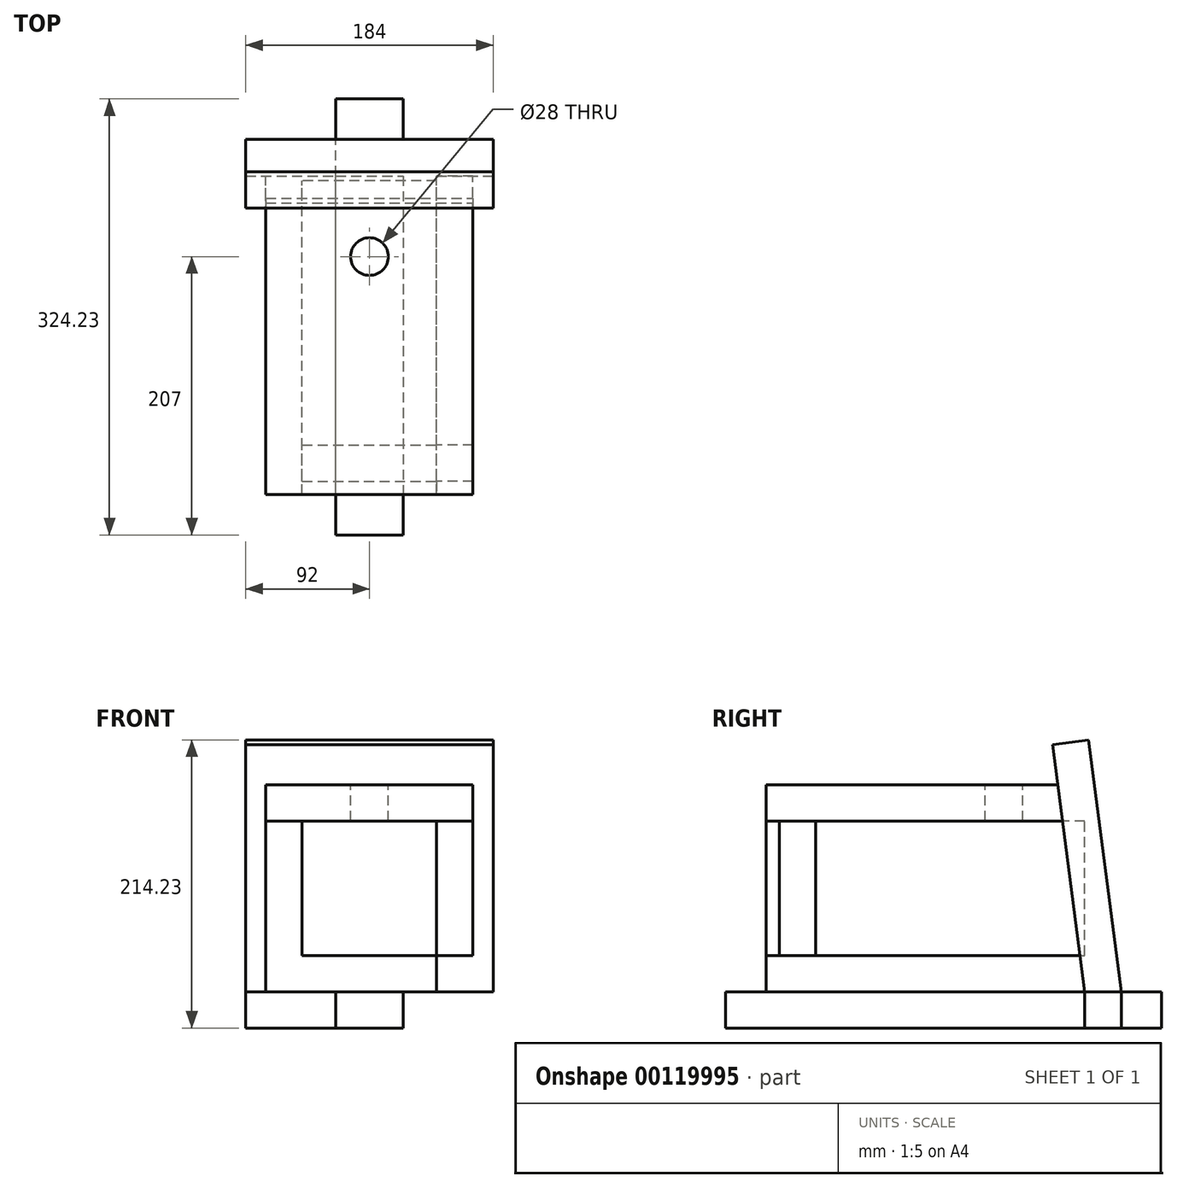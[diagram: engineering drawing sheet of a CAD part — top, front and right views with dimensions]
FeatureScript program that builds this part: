
annotation { "Feature Type Name" : "Feature", "Feature Type Description" : "" }
export const myFeature = defineFeature(function(context is Context, id is Id, definition is map)
    precondition{}
    {
        {
            var Q0;
            Q0=qCreatedBy(makeId("Top.planeOp"),FACE);
            var sketch = newSketch(context, id + "F0", { "sketchPlane" : qUnion([Q0])});
            skLineSegment(sketch, "E0.bottom", {"start": v(0, 0) * mm, "end": v(100, 0) * mm});
            skLineSegment(sketch, "E0.top", {"start": v(0, 237) * mm, "end": v(100, 237) * mm});
            skLineSegment(sketch, "E0.left", {"start": v(0, 0) * mm, "end": v(0, 237) * mm});
            skLineSegment(sketch, "E0.right", {"start": v(100, 0) * mm, "end": v(100, 237) * mm});
            skSolve(sketch);
        }
        {
            var Q0;
            Q0 = qSketchRegion(id + "F0", true);
            var Q1;
            Q1=makeQuery(id+"F0.imprint","IMPRINT",FACE,{"disambiguationData":[TD([[makeQuery(id+"F0.imprint","IMPRINT",EDGE,{"derivedFrom":sQuery(id+"F0.wireOp",EDGE,"E0.bottom")}),1.0]])]});
            extrude(context, id + "F1", {"entities" : qUnion([Q0, Q1]), "depth" : 27 * mm});
        }
        {
            var Q0;
            Q0=makeQuery(id+"F1.opExtrude","CAP_FACE",FACE,{"disambiguationData":[OSD([sQuery(id+"F0.wireOp",EDGE,"E0.bottom"),sQuery(id+"F0.wireOp",EDGE,"E0.top"),sQuery(id+"F0.wireOp",EDGE,"E0.left"),sQuery(id+"F0.wireOp",EDGE,"E0.right")])],"isStart":false});
            var sketch = newSketch(context, id + "F2", { "sketchPlane" : qUnion([Q0])});
            skLineSegment(sketch, "E1.bottom", {"start": v(0, 37) * mm, "end": v(100, 37) * mm});
            skLineSegment(sketch, "E1.top", {"start": v(0, 10) * mm, "end": v(100, 10) * mm});
            skLineSegment(sketch, "E1.left", {"start": v(0, 37) * mm, "end": v(0, 10) * mm});
            skLineSegment(sketch, "E1.right", {"start": v(100, 37) * mm, "end": v(100, 10) * mm});
            skSolve(sketch);
        }
        {
            var Q0;
            Q0 = qSketchRegion(id + "F2", true);
            extrude(context, id + "F3", {"entities" : qUnion([Q0]), "depth" : 100 * mm});
        }
        {
            var Q0;
            Q0=makeQuery(id+"F1.opExtrude","SWEPT_FACE",FACE,{"disambiguationData":[OSD([sQuery(id+"F0.wireOp",EDGE,"E0.right")])]});
            var sketch = newSketch(context, id + "F4", { "sketchPlane" : qUnion([Q0])});
            skLineSegment(sketch, "E2.0.0", {"start": v(0, 0) * mm, "end": v(237, 0) * mm});
            skLineSegment(sketch, "E2.0.1", {"start": v(237, 0) * mm, "end": v(237, 27) * mm});
            skLineSegment(sketch, "E2.0.2", {"start": v(237, 27) * mm, "end": v(0, 27) * mm});
            skLineSegment(sketch, "E2.0.3", {"start": v(0, 27) * mm, "end": v(0, 0) * mm});
            skLineSegment(sketch, "E3.0.0", {"start": v(10, 27) * mm, "end": v(37, 27) * mm});
            skLineSegment(sketch, "E3.0.1", {"start": v(37, 27) * mm, "end": v(37, 127) * mm});
            skLineSegment(sketch, "E3.0.2", {"start": v(37, 127) * mm, "end": v(10, 127) * mm});
            skLineSegment(sketch, "E3.0.3", {"start": v(10, 127) * mm, "end": v(10, 27) * mm});
            skLineSegment(sketch, "E4.bottom", {"start": v(237, 0) * mm, "end": v(0, 0) * mm});
            skLineSegment(sketch, "E4.top", {"start": v(237, 127) * mm, "end": v(0, 127) * mm});
            skLineSegment(sketch, "E4.left", {"start": v(237, 0) * mm, "end": v(237, 127) * mm});
            skLineSegment(sketch, "E4.right", {"start": v(0, 0) * mm, "end": v(0, 127) * mm});
            skSolve(sketch);
        }
        {
            var Q0;
            {var subQ1=sQuery(id+"F4.wireOp",EDGE,"E3.0.0");Q0=makeQuery(id+"F4.imprint","IMPRINT",FACE,{"disambiguationData":[TD([[makeQuery(id+"F4.imprint","IMPRINT",EDGE,{"derivedFrom":subQ1}),-1.0]])]});}
            var Q1;
            {var subQ3=sQuery(id+"F4.wireOp",EDGE,"E3.0.1");Q1=makeQuery(id+"F4.imprint","IMPRINT",FACE,{"disambiguationData":[TD([[makeQuery(id+"F4.imprint","IMPRINT",EDGE,{"derivedFrom":subQ3}),-1.0]])]});}
            var Q2;
            Q2=makeQuery(id+"F4.imprint","IMPRINT",FACE,{"disambiguationData":[TD([[makeQuery(id+"F4.imprint","IMPRINT",EDGE,{"derivedFrom":sQuery(id+"F4.wireOp",EDGE,"E3.0.0")}),1.0]])]});
            var Q3;
            {var subQ3=sQuery(id+"F4.wireOp",EDGE,"E3.0.3");Q3=makeQuery(id+"F4.imprint","IMPRINT",FACE,{"disambiguationData":[TD([[makeQuery(id+"F4.imprint","IMPRINT",EDGE,{"derivedFrom":subQ3}),-1.0]])]});}
            extrude(context, id + "F5", {"entities" : qUnion([Q0, Q1, Q2, Q3]), "depth" : 27 * mm});
        }
        {
            var Q0;
            Q0=makeQuery(id+"F5.opExtrude","SWEPT_FACE",FACE,{"disambiguationData":[OSD([sQuery(id+"F4.wireOp",EDGE,"E4.top")])]});
            var sketch = newSketch(context, id + "F6", { "sketchPlane" : qUnion([Q0])});
            skLineSegment(sketch, "E5.bottom", {"start": v(127, 237) * mm, "end": v(-27, 237) * mm});
            skLineSegment(sketch, "E5.top", {"start": v(127, 0) * mm, "end": v(-27, 0) * mm});
            skLineSegment(sketch, "E5.left", {"start": v(127, 237) * mm, "end": v(127, 0) * mm});
            skLineSegment(sketch, "E5.right", {"start": v(-27, 237) * mm, "end": v(-27, 0) * mm});
            skSolve(sketch);
        }
        {
            var Q0;
            {var subQ2=sQuery(id+"F6.wireOp",EDGE,"E5.left");Q0=makeQuery(id+"F6.imprint","IMPRINT",FACE,{"disambiguationData":[TD([[makeQuery(id+"F6.imprint","IMPRINT",EDGE,{"derivedFrom":subQ2}),-1.0]])]});}
            var Q1;
            {var subQ2=sQuery(id+"F6.wireOp",EDGE,"E5.right");Q1=makeQuery(id+"F6.imprint","IMPRINT",FACE,{"disambiguationData":[TD([[makeQuery(id+"F6.imprint","IMPRINT",EDGE,{"derivedFrom":subQ2}),1.0]])]});}
            extrude(context, id + "F7", {"entities" : qUnion([Q0, Q1]), "depth" : 27 * mm});
        }
        {
            var Q0;
            Q0=makeQuery(id+"F7.opExtrude","CAP_FACE",FACE,{"disambiguationData":[OSD([sQuery(id+"F6.wireOp",EDGE,"E5.bottom"),sQuery(id+"F6.wireOp",EDGE,"E5.top"),sQuery(id+"F6.wireOp",EDGE,"E5.left"),sQuery(id+"F6.wireOp",EDGE,"E5.right")])],"isStart":false});
            var sketch = newSketch(context, id + "F8", { "sketchPlane" : qUnion([Q0])});
            skLineSegment(sketch, "E6.0.1", {"start": v(100, 237) * mm, "end": v(100, 0) * mm});
            skLineSegment(sketch, "E6.0.3", {"start": v(100, 0) * mm, "end": v(100, 237) * mm});
            skLineSegment(sketch, "E7.0.0", {"start": v(0, 37) * mm, "end": v(0, 10) * mm});
            skLineSegment(sketch, "E7.0.2", {"start": v(0, 10) * mm, "end": v(0, 37) * mm});
            skCircle(sketch, "E8", {"center": v(50, 177) * mm, "radius": 14 * mm});
            skPoint(sketch, "E8.centerSnap0", {"position": v(50, 0) * mm});
            skSolve(sketch);
        }
        {
            var Q0;
            Q0=makeQuery(id+"F8.imprint","IMPRINT",FACE,{"disambiguationData":[TD([[makeQuery(id+"F8.imprint","IMPRINT",EDGE,{"derivedFrom":sQuery(id+"F8.wireOp",EDGE,"E8")}),1.0]])]});
            extrude(context, id + "F9", {"entities" : qUnion([Q0]), "operationType" : NewBodyOperationType.REMOVE, "endBound" : BoundingType.UP_TO_NEXT, "oppositeDirection" : true, "depth" : 25 * mm});
        }
        {
            var Q0;
            Q0=makeQuery(id+"F5.opExtrude","CAP_FACE",FACE,{"disambiguationData":[OSD([sQuery(id+"F4.wireOp",EDGE,"E4.bottom"),sQuery(id+"F4.wireOp",EDGE,"E4.top"),sQuery(id+"F4.wireOp",EDGE,"E4.left"),sQuery(id+"F4.wireOp",EDGE,"E4.right")])],"isStart":false});
            var sketch = newSketch(context, id + "F10", { "sketchPlane" : qUnion([Q0])});
            skLineSegment(sketch, "E9.0.0", {"start": v(0, 127) * mm, "end": v(237, 127) * mm});
            skLineSegment(sketch, "E9.0.1", {"start": v(237, 127) * mm, "end": v(237, 154) * mm});
            skLineSegment(sketch, "E9.0.2", {"start": v(237, 154) * mm, "end": v(0, 154) * mm});
            skLineSegment(sketch, "E9.0.3", {"start": v(0, 154) * mm, "end": v(0, 127) * mm});
            skLineSegment(sketch, "E10.0.0", {"start": v(237, 0) * mm, "end": v(237, 127) * mm});
            skLineSegment(sketch, "E10.0.1", {"start": v(237, 127) * mm, "end": v(0, 127) * mm});
            skLineSegment(sketch, "E10.0.2", {"start": v(0, 127) * mm, "end": v(0, 0) * mm});
            skLineSegment(sketch, "E10.0.3", {"start": v(0, 0) * mm, "end": v(237, 0) * mm});
            skLineSegment(sketch, "E11", {"start": v(237, 0) * mm, "end": v(217, 154) * mm});
            skSolve(sketch);
        }
        {
            var Q0;
            {var subQ0=sQuery(id+"F10.wireOp",EDGE,"E10.0.0");Q0=makeQuery(id+"F10.imprint","IMPRINT",FACE,{"disambiguationData":[TD([[makeQuery(id+"F10.imprint","IMPRINT",EDGE,{"derivedFrom":subQ0}),-1.0]])]});}
            var Q1;
            {var subQ0=sQuery(id+"F10.wireOp",EDGE,"E9.0.1");Q1=makeQuery(id+"F10.imprint","IMPRINT",FACE,{"disambiguationData":[TD([[makeQuery(id+"F10.imprint","IMPRINT",EDGE,{"derivedFrom":subQ0}),1.0]])]});}
            extrude(context, id + "F11", {"entities" : qUnion([Q0, Q1]), "operationType" : NewBodyOperationType.REMOVE, "endBound" : BoundingType.THROUGH_ALL, "oppositeDirection" : true, "depth" : 25 * mm});
        }
        {
            var Q0;
            Q0=makeQuery(id+"F1.opExtrude","SWEPT_FACE",FACE,{"disambiguationData":[OSD([sQuery(id+"F0.wireOp",EDGE,"E0.left")])]});
            var sketch = newSketch(context, id + "F12", { "sketchPlane" : qUnion([Q0])});
            skLineSegment(sketch, "E12.0.0", {"start": v(-220.5, 127) * mm, "end": v(-237, 0) * mm});
            skLineSegment(sketch, "E12.0.1", {"start": v(-237, 0) * mm, "end": v(0, 0) * mm});
            skLineSegment(sketch, "E12.0.2", {"start": v(0, 0) * mm, "end": v(0, 127) * mm});
            skLineSegment(sketch, "E12.0.3", {"start": v(0, 127) * mm, "end": v(-220.5, 127) * mm});
            skSolve(sketch);
        }
        {
            var Q0;
            {var subQ2=sQuery(id+"F12.wireOp",EDGE,"E12.0.3");Q0=makeQuery(id+"F12.imprint","IMPRINT",FACE,{"disambiguationData":[TD([[makeQuery(id+"F12.imprint","IMPRINT",EDGE,{"derivedFrom":subQ2}),1.0]])]});}
            var Q1;
            {var subQ0=sQuery(id+"F12.wireOp",EDGE,"E12.0.1");Q1=makeQuery(id+"F12.imprint","IMPRINT",FACE,{"disambiguationData":[TD([[makeQuery(id+"F12.imprint","IMPRINT",EDGE,{"derivedFrom":subQ0}),-1.0]])]});}
            extrude(context, id + "F13", {"entities" : qUnion([Q0, Q1]), "depth" : 27 * mm});
        }
        {
            var Q0;
            Q0=makeQuery(id+"F13.opExtrude","SWEPT_FACE",FACE,{"disambiguationData":[OSD([sQuery(id+"F12.wireOp",EDGE,"E12.0.0")])]});
            var sketch = newSketch(context, id + "F14", { "sketchPlane" : qUnion([Q0])});
            skLineSegment(sketch, "E13.0.0", {"start": v(27, 97.54) * mm, "end": v(27, 124.77) * mm});
            skLineSegment(sketch, "E13.0.1", {"start": v(27, 124.77) * mm, "end": v(-127, 124.77) * mm});
            skLineSegment(sketch, "E13.0.2", {"start": v(-127, 124.77) * mm, "end": v(-127, 97.54) * mm});
            skLineSegment(sketch, "E13.0.3", {"start": v(-127, 97.54) * mm, "end": v(27, 97.54) * mm});
            skLineSegment(sketch, "E14.0.0", {"start": v(-100, 97.54) * mm, "end": v(-127, 97.54) * mm});
            skLineSegment(sketch, "E14.0.1", {"start": v(-127, 97.54) * mm, "end": v(-127, -30.52) * mm});
            skLineSegment(sketch, "E14.0.2", {"start": v(-127, -30.52) * mm, "end": v(-100, -30.52) * mm});
            skLineSegment(sketch, "E14.0.3", {"start": v(-100, -30.52) * mm, "end": v(-100, 97.54) * mm});
            skLineSegment(sketch, "E15.0.0", {"start": v(0, -3.3) * mm, "end": v(-100, -3.3) * mm});
            skLineSegment(sketch, "E15.0.1", {"start": v(-100, -3.3) * mm, "end": v(-100, -30.52) * mm});
            skLineSegment(sketch, "E15.0.2", {"start": v(-100, -30.52) * mm, "end": v(0, -30.52) * mm});
            skLineSegment(sketch, "E15.0.3", {"start": v(0, -30.52) * mm, "end": v(0, -3.3) * mm});
            skLineSegment(sketch, "E16.0.0", {"start": v(0, 97.54) * mm, "end": v(0, -30.52) * mm});
            skLineSegment(sketch, "E16.0.1", {"start": v(0, -30.52) * mm, "end": v(27, -30.52) * mm});
            skLineSegment(sketch, "E16.0.2", {"start": v(27, -30.52) * mm, "end": v(27, 97.54) * mm});
            skLineSegment(sketch, "E16.0.3", {"start": v(27, 97.54) * mm, "end": v(0, 97.54) * mm});
            skLineSegment(sketch, "E17.bottom", {"start": v(27, -30.52) * mm, "end": v(-127, -30.52) * mm});
            skLineSegment(sketch, "E17.left", {"start": v(27, -30.52) * mm, "end": v(27, 124.77) * mm});
            skLineSegment(sketch, "E17.right", {"start": v(-127, -30.52) * mm, "end": v(-127, 124.77) * mm});
            skLineSegment(sketch, "E18.bottom", {"start": v(42, -30.52) * mm, "end": v(-142, -30.52) * mm});
            skLineSegment(sketch, "E18.top", {"start": v(42, 154.77) * mm, "end": v(-142, 154.77) * mm});
            skLineSegment(sketch, "E18.left", {"start": v(42, -30.52) * mm, "end": v(42, 154.77) * mm});
            skLineSegment(sketch, "E18.right", {"start": v(-142, -30.52) * mm, "end": v(-142, 154.77) * mm});
            skSolve(sketch);
        }
        {
            var Q0;
            Q0 = qSketchRegion(id + "F14", true);
            var Q1;
            Q1=makeQuery(id+"F14.imprint","IMPRINT",FACE,{"disambiguationData":[TD([[makeQuery(id+"F14.imprint","IMPRINT",EDGE,{"derivedFrom":sQuery(id+"F14.wireOp",EDGE,"E13.0.3")}),1.0]])]});
            var Q2;
            {var subQ0=sQuery(id+"F14.wireOp",EDGE,"E13.0.3");Q2=makeQuery(id+"F14.imprint","IMPRINT",FACE,{"disambiguationData":[TD([[makeQuery(id+"F14.imprint","IMPRINT",EDGE,{"derivedFrom":subQ0}),-1.0]])]});}
            extrude(context, id + "F15", {"entities" : qUnion([Q0, Q1, Q2]), "depth" : 27 * mm});
        }
        {
            var Q0;
            Q0=makeQuery(id+"F15.opExtrude","SWEPT_FACE",FACE,{"disambiguationData":[OSD([sQuery(id+"F14.wireOp",EDGE,"E18.left")])]});
            var sketch = newSketch(context, id + "F16", { "sketchPlane" : qUnion([Q0])});
            skLineSegment(sketch, "E19.0.0", {"start": v(-237, 0) * mm, "end": v(-213.14, 183.75) * mm});
            skLineSegment(sketch, "E19.0.1", {"start": v(-213.14, 183.75) * mm, "end": v(-239.91, 187.23) * mm});
            skLineSegment(sketch, "E19.0.2", {"start": v(-239.91, 187.23) * mm, "end": v(-263.78, 3.48) * mm});
            skLineSegment(sketch, "E19.0.3", {"start": v(-263.78, 3.48) * mm, "end": v(-237, 0) * mm});
            skLineSegment(sketch, "E20", {"start": v(-237, 0) * mm, "end": v(-264.23, 0) * mm});
            skLineSegment(sketch, "E21", {"start": v(-263.78, 3.48) * mm, "end": v(-264.23, 0) * mm});
            skPoint(sketch, "E22.orphan", {"position": v(-263.78, 0) * mm});
            skSolve(sketch);
        }
        {
            var Q0;
            Q0=makeQuery(id+"F16.imprint","IMPRINT",FACE,{"disambiguationData":[TD([[makeQuery(id+"F16.imprint","IMPRINT",EDGE,{"derivedFrom":sQuery(id+"F16.wireOp",EDGE,"E19.0.3")}),-1.0]])]});
            var Q1;
            Q1=makeQuery(id+"F15.opExtrude","SWEPT_FACE",FACE,{"disambiguationData":[OSD([sQuery(id+"F14.wireOp",EDGE,"E18.right")])]});
            extrude(context, id + "F17", {"entities" : qUnion([Q0]), "operationType" : NewBodyOperationType.ADD, "endBound" : BoundingType.UP_TO_SURFACE, "oppositeDirection" : true, "endBoundEntityFace" : qUnion([Q1]), "depth" : 25 * mm});
        }
        {
            var Q0;
            Q0=makeQuery(id+"F1.opExtrude","CAP_FACE",FACE,{"disambiguationData":[OSD([sQuery(id+"F0.wireOp",EDGE,"E0.bottom"),sQuery(id+"F0.wireOp",EDGE,"E0.top"),sQuery(id+"F0.wireOp",EDGE,"E0.left"),sQuery(id+"F0.wireOp",EDGE,"E0.right")])],"isStart":true});
            var sketch = newSketch(context, id + "F18", { "sketchPlane" : qUnion([Q0])});
            skLineSegment(sketch, "E23.0.0", {"start": v(0, 0) * mm, "end": v(0, -237) * mm});
            skLineSegment(sketch, "E23.0.1", {"start": v(0, -237) * mm, "end": v(100, -237) * mm});
            skLineSegment(sketch, "E23.0.2", {"start": v(100, -237) * mm, "end": v(100, 0) * mm});
            skLineSegment(sketch, "E23.0.3", {"start": v(100, 0) * mm, "end": v(0, 0) * mm});
            skLineSegment(sketch, "E24.0.0", {"start": v(142, -264.23) * mm, "end": v(142, -237) * mm});
            skLineSegment(sketch, "E24.0.1", {"start": v(142, -237) * mm, "end": v(-42, -237) * mm});
            skLineSegment(sketch, "E24.0.2", {"start": v(-42, -237) * mm, "end": v(-42, -264.23) * mm});
            skLineSegment(sketch, "E24.0.3", {"start": v(-42, -264.23) * mm, "end": v(142, -264.23) * mm});
            skLineSegment(sketch, "E25.0", {"start": v(25, 30) * mm, "end": v(25, -294.23) * mm});
            skLineSegment(sketch, "E25.1", {"start": v(75, 30) * mm, "end": v(25, 30) * mm});
            skLineSegment(sketch, "E25.2", {"start": v(75, -294.23) * mm, "end": v(75, 30) * mm});
            skLineSegment(sketch, "E25.3", {"start": v(25, -294.23) * mm, "end": v(75, -294.23) * mm});
            skSolve(sketch);
        }
        {
            var Q0;
            {var subQ0=sQuery(id+"F18.wireOp",EDGE,"E25.0");var subQ1=sQuery(id+"F18.wireOp",EDGE,"E23.0.3");var subQ2=makeQuery(id+"F18.imprint","INTERSECT",VERTEX,{"derivedFrom":[subQ1,subQ0]});Q0=makeQuery(id+"F18.imprint","IMPRINT",FACE,{"disambiguationData":[TD([[makeQuery(id+"F18.imprint","IMPRINT",EDGE,{"disambiguationData":[TD([[subQ2,-1.0]])],"derivedFrom":subQ1}),-1.0]])]});}
            var Q1;
            {var subQ0=sQuery(id+"F18.wireOp",EDGE,"E25.0");var subQ1=sQuery(id+"F18.wireOp",EDGE,"E24.0.1");var subQ2=makeQuery(id+"F18.imprint","INTERSECT",VERTEX,{"derivedFrom":[subQ1,subQ0]});Q1=makeQuery(id+"F18.imprint","IMPRINT",FACE,{"disambiguationData":[TD([[makeQuery(id+"F18.imprint","IMPRINT",EDGE,{"disambiguationData":[TD([[subQ2,-1.0]])],"derivedFrom":subQ1}),-1.0]])]});}
            var Q2;
            {var subQ5=sQuery(id+"F18.wireOp",EDGE,"E25.3");Q2=makeQuery(id+"F18.imprint","IMPRINT",FACE,{"disambiguationData":[TD([[makeQuery(id+"F18.imprint","IMPRINT",EDGE,{"derivedFrom":subQ5}),1.0]])]});}
            var Q3;
            {var subQ5=sQuery(id+"F18.wireOp",EDGE,"E25.1");Q3=makeQuery(id+"F18.imprint","IMPRINT",FACE,{"disambiguationData":[TD([[makeQuery(id+"F18.imprint","IMPRINT",EDGE,{"derivedFrom":subQ5}),1.0]])]});}
            extrude(context, id + "F19", {"entities" : qUnion([Q0, Q1, Q2, Q3]), "depth" : 27 * mm});
        }
    });
